# Revit family: Slots AnCar 5
name_source: partatom
category: Lighting Fixtures
revit_build: Autodesk Revit 2017 (Build: 20160225_1515(x64)
units: mm (PartAtom-declared; Revit-internal decimal feet)

## family parameters
Always vertical = Yes
Cut with Voids When Loaded = No
Light Source = Yes
OmniClass Number = 23.80.70.00
OmniClass Title = Lighting
Part Type = Normal
Room Calculation Point = No
Round Connector Dimension = Use Diameter
Shared = No
Work Plane-Based = No

## types (7) — shared parameters
Color Filter = 16777215
Dimming Lamp Color Temperature Shift = <None>
Light Source Symbol Size = 0' - 5 1/4"
width = 0' - 5 1/4"

## per-type parameters (varying)
| type | Emit from Line Length | Length |
| 2ft nominal 5in | 1' - 11" | 1' - 11" |
| 3ft nominal 5in | 2' - 11" | 2' - 11" |
| 4ft nominal 5in | 3' - 11" | 3' - 11" |
| 5ft nominal 5in | 4' - 11" | 4' - 11" |
| 6ft nominal 5in | 5' - 11" | 5' - 11" |
| 7ft nominal 5in | 6' - 11" | 6' - 11" |
| 8ft nominal 5in | 7' - 11" | 7' - 11" |

## geometry (parser evidence)
native form markers: Extrusion x1, Sweep x2
no freeform markers — native parametric forms only
